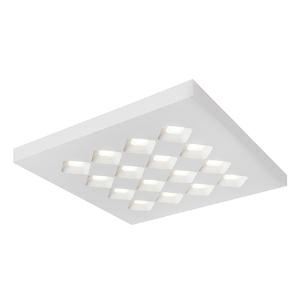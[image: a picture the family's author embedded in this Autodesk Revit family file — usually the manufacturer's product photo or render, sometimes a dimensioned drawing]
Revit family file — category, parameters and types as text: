
# Revit family: 3f_filippi_-_3f_diagon_p_soft_ugr_tunable_white_3f_filippi_-_12142_-_3f_diagon_p_25w_dt8_tw_soft_ugr_596_9e28a5f2c8edde2d
name_source: partatom
category: Lighting Fixtures
units: mm (PartAtom-declared; Revit-internal decimal feet)

## family parameters
Cut with Voids When Loaded = No
Host = Face
Light Source = No
Part Type = Normal
Room Calculation Point = No
Round Connector Dimension = Use Diameter
Shared = No

## types (1)
- 3F Filippi - 3F Dìagon P Soft UGR Tunable White (1 x LED, 3567 lm, 29 W, 4000 K)
    Apparent Load = 29 VA
    Approval mark = ENEC
    CIE Flux Codes = 59 92 100 100 100
    Color Rendering = 80
    Color Temperature = 4000 K
    Control Gear = Electronic transformer
    Default Elevation = 1800 mm
    Description = ILLUMINOTECHNICAL
Luminous efficiency 100% (DLOR 100%, ULOR 0%).
Initial luminous flux of the luminaire 3567 lm.
Direct symmetric distribution.
Installation Interdistance Transv.D = 1.23 x hu - Long.D = 1.23 x hu.
Average luminance <3000 cd/m² for radial angles >65°.
Tabular UGR (CIE 117 - 4H-8H; S=0.25H; 70/50/20): RUG 18.6 - 18.6.
Beam angle: 102° - 101°.
Luminous efficacy 123 lm/W.
Lifetime (L95/B10): 30000 h. (tq+25°C)
Lifetime (L90/B10): 50000 h. (tq+25°C)
Lifetime (L80/B10): 80000 h. (tq+25°C)
Lifetime (L75/B10): 100000 h. (tq+25°C)
Sudden decreased luminous flux after 50000 hours: 0% (C0).
Photobiological safety in compliance with IEC/TR 62778: RG0 risk exempt, (IEC 62471).
In compliance with IEC/EN 62722-2-1 - IEC/EN 62717 standards.

SOURCE
Squared LED module 25W/TW.
Energy efficiency class (UE 2019/2020 - UE 2019/2015): D.
CIE 13.3 Colour rendering index: CRI >80 (R9 <50%).
IES TM-30 Fidelity Index: Rf = 84 Rg = 95.
The colour temperature can be adjusted between 2700 K and 6500 K.
Colour initial tolerance (MacAdam): SDCM 3.

MECHANICAL
White painted frame.
Height only 40 mm.
Housing in hot-galvanised steel, painted in white polyester.
Honeycombed diagonal screen in white anti-glare polycarbonate.
Opal methacrylate (PMMA) rhomboid lenses with differentiated, engraved and prismatic surfaces for diffused, soft lighting and excellent visual comfort.
Luminaire with limited surface temperature. - D - (EN 60598-2-24)
Dimensions: 596x596 mm, height 40 mm. Weight 6.825 kg.
IP40 protection degree.
Mechanical strength to impacts IK06 (1 joule).
Glow-wire test resistance 650°C.

ELECTRICAL
Halogen Free DALI DT8, PUSH-DIM, electronic wiring 230V-50/60Hz, power factor 0.90 at full load, THD <25%, constant output current, class I, 1 driver, 1 DALI addresse.
Power of the luminaire 29 W.
CE - IEC 60598-1 - EN 60598-1.
SAFE FLICKER: PstLM=<1 and SVM=<0.4 (IEC TR 61547-1 and IEC TR 63158), to ensure a more comfortable and safe light.
Luminaire compliant with EN 60598-2-22 for power supply from a centralised emergency system CPSS (Central Power Supply System), not incorporated in the luminaire - high risk areas excluded. The default power and flux are 100% in AC and 15% in DC.
Ambient temperature from 0°C to +25°C.
Temperature class T6 max 85°C.
5-pole terminal block (L-N-PE-DA/DA) quick connection for line connection with connection capacity 2x2.5 mm² per poles.
Relative humidity UR: <85%.

INSTALLATION
Ceiling.

APPLICATIONS
Any environments requiring light which aims for the wellness of people.
Environments: staterooms, with VDTs, offices.
Environments with exacting visual tasks, where diffused soft light for optimum visual comfort is required.

LIGHT MANAGEMENT
Recommended minimum setting: 10%.
The luminaire, equipped with DALI DT8 driver, is designed for adjusting the luminous flux and colour temperature; can be controlled manually or automatically/manually with 3F HCL technology or 3F Bluetooth.

WARNING
Luminaire designed for disposal/recycling at end-of-life.
Replaceable (LED only) light source by a professional. Replaceable control gear by a professional.
    Height = 40 mm  [stored 0.131234 ft]
    Lamp = 1 x LED
    Lamp Light Flux = 3567 lm
    Lamp Power = 29 W
    Lamp count = 1
    Length = 596 mm
    Lifetime = 50000 h
    Luminous efficacy = 123 lm/W
    Manufacturer = 3F Filippi
    ModVariant = No
    Model = 3F Filippi - 12142 - 3F Diagon P 25W DT8 TW SOFT UGR 596x596 (CCT 4000)
    Mounting Place = Ceiling
    Mounting Type = Surface mounted
    Number of Poles = 1
    OnlyDefault = Yes
    Power Factor = 1
    Product Name = 3F Filippi - 3F Dìagon P Soft UGR Tunable White
    Product group = ceiling mounted luminaire
    ProductGroupID = 3
    Protection Class = Protection class I
    Protection Degree = IP 40
    RLX_Detail_Level = 1
    RLX_Emergency_Light_Flux = 0 lm
    RLX_Emergency_Type = 0
    RLX_Emergency_Type_DB = No
    RlxData = <blob elided: 97169 chars, md5=0a040a69>
    Socket = socket
    Standby Power = 0 W
    System Light Flux = 3567 lm
    System Power = 29 W
    Type Comments = Product without accessories
    Type Image = 3ffilippi_3f_diagon_p_soft_ugr_tunable_white.jpg
    URL = http://relux.com
    VarID = ---
    Voltage = 0 V
    Weight = 0.00 kg
    Width = 596 mm

note: [stored X ft] marks values corroborated as IEEE doubles in the binary element streams (Revit-internal decimal feet)

## geometry (parser evidence)
native form markers: Blend x4, Sweep x9
no freeform markers — native parametric forms only
